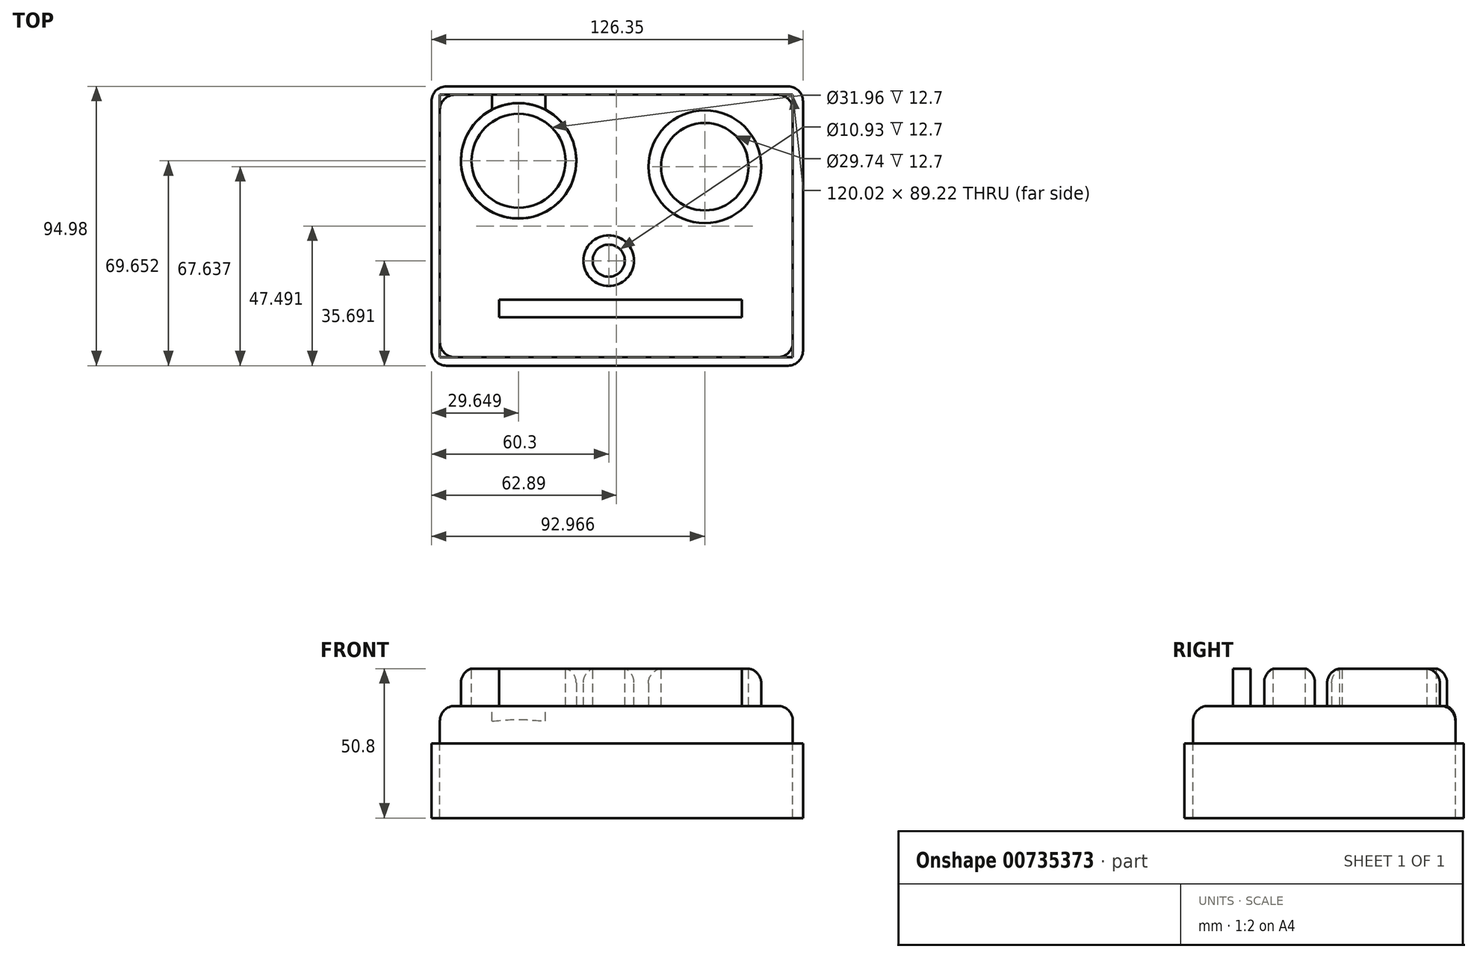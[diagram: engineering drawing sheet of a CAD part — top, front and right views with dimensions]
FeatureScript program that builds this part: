
annotation { "Feature Type Name" : "Feature", "Feature Type Description" : "" }
export const myFeature = defineFeature(function(context is Context, id is Id, definition is map)
    precondition{}
    {
        {
            var Q0;
            Q0=qCreatedBy(makeId("Top.planeOp"),FACE);
            var sketch = newSketch(context, id + "F0", { "sketchPlane" : qUnion([Q0])});
            skLineSegment(sketch, "E0.bottom", {"start": v(-60.3, 49.36) * mm, "end": v(66.05, 49.36) * mm});
            skLineSegment(sketch, "E0.top", {"start": v(-60.3, -45.62) * mm, "end": v(66.05, -45.62) * mm});
            skLineSegment(sketch, "E0.left", {"start": v(-60.3, 49.36) * mm, "end": v(-60.3, -45.62) * mm});
            skLineSegment(sketch, "E0.right", {"start": v(66.05, 49.36) * mm, "end": v(66.05, -45.62) * mm});
            skSolve(sketch);
        }
        {
            var Q0;
            Q0 = qSketchRegion(id + "F0", true);
            extrude(context, id + "F1", {"entities" : qUnion([Q0]), "depth" : 25.4 * mm, "offsetDistance" : 25.4 * mm});
        }
        {
            var Q0;
            Q0=makeQuery(id+"F1.opExtrude","CAP_FACE",FACE,{"disambiguationData":[OSD([sQuery(id+"F0.wireOp",EDGE,"E0.bottom"),sQuery(id+"F0.wireOp",EDGE,"E0.top"),sQuery(id+"F0.wireOp",EDGE,"E0.left"),sQuery(id+"F0.wireOp",EDGE,"E0.right")])],"isStart":false});
            var sketch = newSketch(context, id + "F2", { "sketchPlane" : qUnion([Q0])});
            skLineSegment(sketch, "E1.bottom", {"start": v(-57.42, 46.48) * mm, "end": v(62.6, 46.48) * mm});
            skLineSegment(sketch, "E1.top", {"start": v(-57.42, -42.74) * mm, "end": v(62.6, -42.74) * mm});
            skLineSegment(sketch, "E1.left", {"start": v(-57.42, 46.48) * mm, "end": v(-57.42, -42.74) * mm});
            skLineSegment(sketch, "E1.right", {"start": v(62.6, 46.48) * mm, "end": v(62.6, -42.74) * mm});
            skSolve(sketch);
        }
        {
            var Q0;
            Q0 = qSketchRegion(id + "F2", true);
            extrude(context, id + "F3", {"entities" : qUnion([Q0]), "operationType" : NewBodyOperationType.REMOVE, "oppositeDirection" : true, "depth" : 25.4 * mm, "offsetDistance" : 25.4 * mm});
        }
        {
            var Q0;
            Q0=makeQuery(id+"F1.opExtrude","CAP_FACE",FACE,{"disambiguationData":[OSD([sQuery(id+"F0.wireOp",EDGE,"E0.bottom"),sQuery(id+"F0.wireOp",EDGE,"E0.top"),sQuery(id+"F0.wireOp",EDGE,"E0.left"),sQuery(id+"F0.wireOp",EDGE,"E0.right")])],"isStart":false});
            var sketch = newSketch(context, id + "F4", { "sketchPlane" : qUnion([Q0])});
            skLineSegment(sketch, "E2.bottom", {"start": v(-57.42, 46.48) * mm, "end": v(62.6, 46.48) * mm});
            skLineSegment(sketch, "E2.top", {"start": v(-57.42, -42.74) * mm, "end": v(62.6, -42.74) * mm});
            skLineSegment(sketch, "E2.left", {"start": v(-57.42, 46.48) * mm, "end": v(-57.42, -42.74) * mm});
            skLineSegment(sketch, "E2.right", {"start": v(62.6, 46.48) * mm, "end": v(62.6, -42.74) * mm});
            skSolve(sketch);
        }
        {
            var Q0;
            Q0 = qSketchRegion(id + "F4", true);
            extrude(context, id + "F5", {"entities" : qUnion([Q0]), "depth" : 12.7 * mm, "offsetDistance" : 25.4 * mm});
        }
        {
            var Q0;
            Q0=makeQuery(id+"F5.opExtrude","CAP_FACE",FACE,{"disambiguationData":[OSD([sQuery(id+"F4.wireOp",EDGE,"E2.bottom"),sQuery(id+"F4.wireOp",EDGE,"E2.top"),sQuery(id+"F4.wireOp",EDGE,"E2.left"),sQuery(id+"F4.wireOp",EDGE,"E2.right")])],"isStart":false});
            var sketch = newSketch(context, id + "F6", { "sketchPlane" : qUnion([Q0])});
            skCircle(sketch, "E3", {"center": v(-30.65, 24.03) * mm, "radius": 19.6 * mm});
            skSolve(sketch);
        }
        {
            var Q0;
            Q0 = qSketchRegion(id + "F6", true);
            extrude(context, id + "F7", {"entities" : qUnion([Q0]), "operationType" : NewBodyOperationType.ADD, "depth" : 12.7 * mm, "offsetDistance" : 25.4 * mm});
        }
        {
            var Q0;
            Q0=makeQuery(id+"F7.opExtrude","CAP_FACE",FACE,{"disambiguationData":[OSD([sQuery(id+"F6.wireOp",EDGE,"E3")])],"isStart":false});
            var sketch = newSketch(context, id + "F8", { "sketchPlane" : qUnion([Q0])});
            skCircle(sketch, "E4", {"center": v(-30.65, 24.03) * mm, "radius": 15.98 * mm});
            skSolve(sketch);
        }
        {
            var Q0;
            Q0 = qSketchRegion(id + "F8", true);
            extrude(context, id + "F9", {"entities" : qUnion([Q0]), "operationType" : NewBodyOperationType.REMOVE, "oppositeDirection" : true, "depth" : 12.7 * mm, "offsetDistance" : 25.4 * mm});
        }
        {
            var Q0;
            Q0=makeQuery(id+"F5.opExtrude","CAP_FACE",FACE,{"disambiguationData":[OSD([sQuery(id+"F4.wireOp",EDGE,"E2.bottom"),sQuery(id+"F4.wireOp",EDGE,"E2.top"),sQuery(id+"F4.wireOp",EDGE,"E2.left"),sQuery(id+"F4.wireOp",EDGE,"E2.right")])],"isStart":false});
            var sketch = newSketch(context, id + "F10", { "sketchPlane" : qUnion([Q0])});
            skSolve(sketch);
        }
        {
            var Q0;
            Q0=makeQuery(id+"F7.opExtrude","CAP_EDGE",EDGE,{"disambiguationData":[OSD([sQuery(id+"F6.wireOp",EDGE,"E3")])],"isStart":false});
            fillet(context, id + "F11", {"entities" : qUnion([Q0]), "radius" : 5.08 * mm, "tangentPropagation" : true, "allowEdgeOverflow" : false});
        }
        {
            var Q0;
            Q0=makeQuery(id+"F5.opExtrude","CAP_EDGE",EDGE,{"disambiguationData":[OSD([sQuery(id+"F4.wireOp",EDGE,"E2.left")])],"isStart":false});
            var Q1;
            Q1=makeQuery(id+"F5.opExtrude","CAP_EDGE",EDGE,{"disambiguationData":[OSD([sQuery(id+"F4.wireOp",EDGE,"E2.top")])],"isStart":false});
            var Q2;
            Q2=makeQuery(id+"F5.opExtrude","CAP_EDGE",EDGE,{"disambiguationData":[OSD([sQuery(id+"F4.wireOp",EDGE,"E2.bottom")])],"isStart":false});
            var Q3;
            Q3=makeQuery(id+"F5.opExtrude","CAP_EDGE",EDGE,{"disambiguationData":[OSD([sQuery(id+"F4.wireOp",EDGE,"E2.right")])],"isStart":false});
            fillet(context, id + "F12", {"entities" : qUnion([Q0, Q1, Q2, Q3]), "radius" : 5.08 * mm, "tangentPropagation" : true, "allowEdgeOverflow" : false});
        }
        {
            var Q0;
            Q0=makeQuery(id+"F5.opExtrude","SWEPT_EDGE",EDGE,{"disambiguationData":[OSD([sQuery(id+"F4.wireOp",EDGE,"E2.top"),sQuery(id+"F4.wireOp",EDGE,"E2.left")])]});
            var Q1;
            Q1=makeQuery(id+"F5.opExtrude","SWEPT_EDGE",EDGE,{"disambiguationData":[OSD([sQuery(id+"F4.wireOp",EDGE,"E2.bottom"),sQuery(id+"F4.wireOp",EDGE,"E2.left")])]});
            var Q2;
            Q2=makeQuery(id+"F5.opExtrude","SWEPT_EDGE",EDGE,{"disambiguationData":[OSD([sQuery(id+"F4.wireOp",EDGE,"E2.bottom"),sQuery(id+"F4.wireOp",EDGE,"E2.right")])]});
            var Q3;
            Q3=makeQuery(id+"F5.opExtrude","SWEPT_EDGE",EDGE,{"disambiguationData":[OSD([sQuery(id+"F4.wireOp",EDGE,"E2.top"),sQuery(id+"F4.wireOp",EDGE,"E2.right")])]});
            fillet(context, id + "F13", {"entities" : qUnion([Q0, Q1, Q2, Q3]), "radius" : 5.08 * mm, "tangentPropagation" : true, "allowEdgeOverflow" : false});
        }
        {
            var Q0;
            Q0=makeQuery(id+"F1.opExtrude","SWEPT_EDGE",EDGE,{"disambiguationData":[OSD([sQuery(id+"F0.wireOp",EDGE,"E0.top"),sQuery(id+"F0.wireOp",EDGE,"E0.right")])]});
            var Q1;
            Q1=makeQuery(id+"F1.opExtrude","SWEPT_EDGE",EDGE,{"disambiguationData":[OSD([sQuery(id+"F0.wireOp",EDGE,"E0.top"),sQuery(id+"F0.wireOp",EDGE,"E0.left")])]});
            var Q2;
            Q2=makeQuery(id+"F1.opExtrude","SWEPT_EDGE",EDGE,{"disambiguationData":[OSD([sQuery(id+"F0.wireOp",EDGE,"E0.bottom"),sQuery(id+"F0.wireOp",EDGE,"E0.left")])]});
            var Q3;
            Q3=makeQuery(id+"F1.opExtrude","SWEPT_EDGE",EDGE,{"disambiguationData":[OSD([sQuery(id+"F0.wireOp",EDGE,"E0.bottom"),sQuery(id+"F0.wireOp",EDGE,"E0.right")])]});
            fillet(context, id + "F14", {"entities" : qUnion([Q0, Q1, Q2, Q3]), "radius" : 5.08 * mm, "tangentPropagation" : true, "allowEdgeOverflow" : false});
        }
        {
            var Q0;
            Q0=makeQuery(id+"F10.imprint","IMPRINT",FACE,{"disambiguationData":[TD([[makeQuery(id+"F10.imprint","IMPRINT",EDGE,{"derivedFrom":makeQuery(id+"F5.opExtrude","CAP_EDGE",EDGE,{"disambiguationData":[OSD([sQuery(id+"F4.wireOp",EDGE,"E2.bottom")])],"isStart":false})}),-1.0]])]});
            var sketch = newSketch(context, id + "F15", { "sketchPlane" : qUnion([Q0])});
            skLineSegment(sketch, "E5.bottom", {"start": v(0, -9.93) * mm, "end": v(3.02, -9.93) * mm});
            skLineSegment(sketch, "E5.top", {"start": v(0, -17.99) * mm, "end": v(3.02, -17.99) * mm});
            skLineSegment(sketch, "E5.left", {"start": v(0, -9.93) * mm, "end": v(0, -17.99) * mm});
            skLineSegment(sketch, "E5.right", {"start": v(3.02, -9.93) * mm, "end": v(3.02, -17.99) * mm});
            skSolve(sketch);
        }
        {
            var Q0;
            Q0 = qSketchRegion(id + "F15", true);
            extrude(context, id + "F16", {"entities" : qUnion([Q0]), "operationType" : NewBodyOperationType.ADD, "depth" : 12.7 * mm, "offsetDistance" : 25.4 * mm});
        }
        {
            var Q0;
            Q0=makeQuery(id+"F16.opExtrude","SWEPT_FACE",FACE,{"disambiguationData":[OSD([sQuery(id+"F15.wireOp",EDGE,"E5.left")])]});
            var Q1;
            Q1=makeQuery(id+"F16.opExtrude","SWEPT_FACE",FACE,{"disambiguationData":[OSD([sQuery(id+"F15.wireOp",EDGE,"E5.top")])]});
            var Q2;
            Q2=makeQuery(id+"F16.opExtrude","SWEPT_EDGE",EDGE,{"disambiguationData":[OSD([sQuery(id+"F15.wireOp",EDGE,"E5.bottom"),sQuery(id+"F15.wireOp",EDGE,"E5.left")])]});
            revolve(context, id + "F17", {"operationType" : NewBodyOperationType.ADD, "surfaceOperationType" : NewSurfaceOperationType.NEW, "entities" : qUnion([Q0, Q1]), "axis" : qUnion([Q2]), "revolveType" : RevolveType.FULL});
        }
        {
            var Q0;
            {var subQ0=sQuery(id+"F15.wireOp",EDGE,"E5.left");var subQ1=sQuery(id+"F15.wireOp",EDGE,"E5.top");Q0=makeQuery(id+"F17.boolean.opBoolean","MERGE",FACE,{"derivedFrom":[makeQuery(id+"F16.opExtrude","CAP_FACE",FACE,{"disambiguationData":[OSD([sQuery(id+"F15.wireOp",EDGE,"E5.bottom"),subQ1,subQ0,sQuery(id+"F15.wireOp",EDGE,"E5.right")])],"isStart":false}),makeQuery(id+"F17.opRevolve","SWEPT_FACE",FACE,{"disambiguationData":[OSD([subQ1]),TDD([makeQuery(id+"F16.opExtrude","CAP_EDGE",EDGE,{"disambiguationData":[OSD([subQ1])],"isStart":false})])]}),makeQuery(id+"F17.opRevolve","SWEPT_FACE",FACE,{"disambiguationData":[OSD([subQ0]),TDD([makeQuery(id+"F16.opExtrude","CAP_EDGE",EDGE,{"disambiguationData":[OSD([subQ0])],"isStart":false})])]})]});}
            var sketch = newSketch(context, id + "F18", { "sketchPlane" : qUnion([Q0])});
            skCircle(sketch, "E6", {"center": v(0, -9.93) * mm, "radius": 5.46 * mm});
            skSolve(sketch);
        }
        {
            var Q0;
            Q0 = qSketchRegion(id + "F18", true);
            extrude(context, id + "F19", {"entities" : qUnion([Q0]), "operationType" : NewBodyOperationType.REMOVE, "oppositeDirection" : true, "depth" : 12.7 * mm, "offsetDistance" : 25.4 * mm});
        }
        {
            var Q0;
            {var subQ0=sQuery(id+"F15.wireOp",EDGE,"E5.right");var subQ1=sQuery(id+"F15.wireOp",EDGE,"E5.top");Q0=makeQuery(id+"F17.opRevolve","SWEPT_EDGE",EDGE,{"disambiguationData":[OSD([subQ1,subQ0]),TDD([makeQuery(id+"F16.opExtrude","CAP_VERTEX",VERTEX,{"disambiguationData":[OSD([subQ1,subQ0])],"isStart":false})])]});}
            fillet(context, id + "F20", {"entities" : qUnion([Q0]), "radius" : 5.08 * mm, "tangentPropagation" : true, "allowEdgeOverflow" : false});
        }
        {
            var Q0;
            Q0=makeQuery(id+"F10.imprint","IMPRINT",FACE,{"disambiguationData":[TD([[makeQuery(id+"F10.imprint","IMPRINT",EDGE,{"derivedFrom":makeQuery(id+"F5.opExtrude","CAP_EDGE",EDGE,{"disambiguationData":[OSD([sQuery(id+"F4.wireOp",EDGE,"E2.bottom")])],"isStart":false})}),-1.0]])]});
            var sketch = newSketch(context, id + "F21", { "sketchPlane" : qUnion([Q0])});
            skCircle(sketch, "E7", {"center": v(32.67, 22.02) * mm, "radius": 19.18 * mm});
            skSolve(sketch);
        }
        {
            var Q0;
            Q0 = qSketchRegion(id + "F21", true);
            extrude(context, id + "F22", {"entities" : qUnion([Q0]), "operationType" : NewBodyOperationType.ADD, "depth" : 12.7 * mm, "offsetDistance" : 25.4 * mm});
        }
        {
            var Q0;
            Q0=makeQuery(id+"F22.opExtrude","CAP_FACE",FACE,{"disambiguationData":[OSD([sQuery(id+"F21.wireOp",EDGE,"E7")])],"isStart":false});
            var sketch = newSketch(context, id + "F23", { "sketchPlane" : qUnion([Q0])});
            skCircle(sketch, "E8", {"center": v(32.67, 22.02) * mm, "radius": 14.87 * mm});
            skSolve(sketch);
        }
        {
            var Q0;
            Q0 = qSketchRegion(id + "F23", true);
            extrude(context, id + "F24", {"entities" : qUnion([Q0]), "operationType" : NewBodyOperationType.REMOVE, "oppositeDirection" : true, "depth" : 12.7 * mm, "offsetDistance" : 25.4 * mm});
        }
        {
            var Q0;
            Q0=makeQuery(id+"F22.opExtrude","CAP_EDGE",EDGE,{"disambiguationData":[OSD([sQuery(id+"F21.wireOp",EDGE,"E7")])],"isStart":false});
            fillet(context, id + "F25", {"entities" : qUnion([Q0]), "radius" : 5.08 * mm, "tangentPropagation" : true, "allowEdgeOverflow" : false});
        }
        {
            var Q0;
            Q0=makeQuery(id+"F10.imprint","IMPRINT",FACE,{"disambiguationData":[TD([[makeQuery(id+"F10.imprint","IMPRINT",EDGE,{"derivedFrom":makeQuery(id+"F5.opExtrude","CAP_EDGE",EDGE,{"disambiguationData":[OSD([sQuery(id+"F4.wireOp",EDGE,"E2.bottom")])],"isStart":false})}),-1.0]])]});
            var sketch = newSketch(context, id + "F26", { "sketchPlane" : qUnion([Q0])});
            skLineSegment(sketch, "E9.bottom", {"start": v(-37.27, -23.17) * mm, "end": v(45.33, -23.17) * mm});
            skLineSegment(sketch, "E9.top", {"start": v(-37.27, -29.21) * mm, "end": v(45.33, -29.21) * mm});
            skLineSegment(sketch, "E9.left", {"start": v(-37.27, -23.17) * mm, "end": v(-37.27, -29.21) * mm});
            skLineSegment(sketch, "E9.right", {"start": v(45.33, -23.17) * mm, "end": v(45.33, -29.21) * mm});
            skSolve(sketch);
        }
        {
            var Q0;
            Q0 = qSketchRegion(id + "F26", true);
            extrude(context, id + "F27", {"entities" : qUnion([Q0]), "operationType" : NewBodyOperationType.ADD, "depth" : 12.7 * mm, "offsetDistance" : 25.4 * mm});
        }
    });
